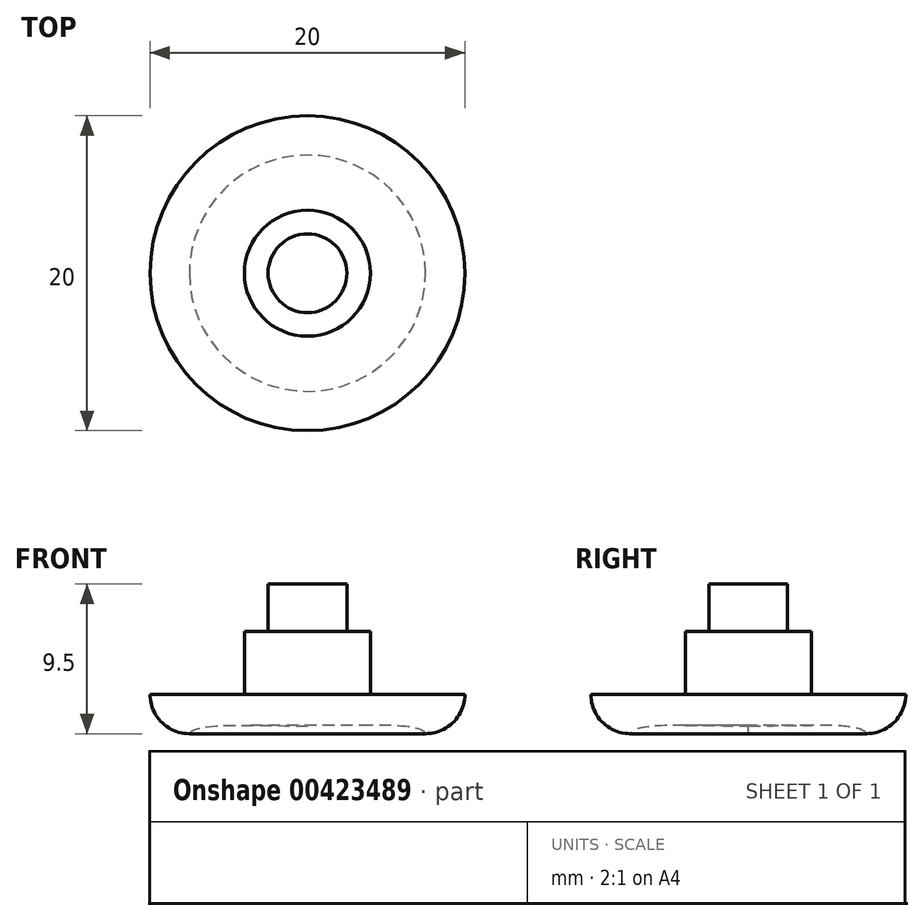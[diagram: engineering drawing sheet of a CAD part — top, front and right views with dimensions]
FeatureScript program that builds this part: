
annotation { "Feature Type Name" : "Feature", "Feature Type Description" : "" }
export const myFeature = defineFeature(function(context is Context, id is Id, definition is map)
    precondition{}
    {
        {
            var Q0;
            Q0=qCreatedBy(makeId("Front.planeOp"),FACE);
            var sketch = newSketch(context, id + "F0", { "sketchPlane" : qUnion([Q0])});
            skLineSegment(sketch, "E0.bottom", {"start": v(-4, 2) * mm, "end": v(4, 2) * mm});
            skLineSegment(sketch, "E0.left", {"start": v(-4, 2) * mm, "end": v(-4, -2) * mm});
            skPoint(sketch, "E0.middle", {"position": v(0, 0) * mm});
            skLineSegment(sketch, "E1", {"start": v(0, 2) * mm, "end": v(0, 5) * mm});
            skPoint(sketch, "E1.endSnap0", {"position": v(0, 2) * mm});
            skLineSegment(sketch, "E2", {"start": v(0, 5) * mm, "end": v(-2.5, 5) * mm});
            skLineSegment(sketch, "E3", {"start": v(-2.5, 5) * mm, "end": v(-2.5, 2) * mm});
            skLineSegment(sketch, "E4", {"start": v(0, -2) * mm, "end": v(-10, -2) * mm});
            skLineSegment(sketch, "E5", {"start": v(0, -2) * mm, "end": v(0, -4) * mm});
            skLineSegment(sketch, "E6", {"start": v(0, 2) * mm, "end": v(0, -2) * mm});
            skLineSegment(sketch, "E7.MirrorCS", {"start": v(0, -2) * mm, "end": v(0, 0) * mm});
            skLineSegment(sketch, "E8", {"start": v(-2.5, 2) * mm, "end": v(0, 2) * mm});
            skLineSegment(sketch, "E9", {"start": v(-10, -2) * mm, "end": v(-10, -2) * mm});
            skPoint(sketch, "E10.visualSharp", {"position": v(-10, -4.5) * mm});
            skArc(sketch, "E10.filletArc", {"start": v(-10, -2) * mm, "mid": v(-9.27, -3.77) * mm, "end": v(-7.5, -4.5) * mm});
            skFitSpline(sketch, "E11", {"points": [v(-7.5, -4.5) * mm, v(0, -4) * mm], "startDerivative": vector(1, 2.2) * mm, "endDerivative": vector(11.01, 0) * mm});
            skSolve(sketch);
        }
        {
            var Q0;
            {var subQ0=sQuery(id+"F0.wireOp",EDGE,"E5");Q0=makeQuery(id+"F0.imprint","IMPRINT",FACE,{"disambiguationData":[TD([[makeQuery(id+"F0.imprint","IMPRINT",EDGE,{"derivedFrom":subQ0}),-1.0]])]});}
            var Q1;
            {var subQ1=sQuery(id+"F0.wireOp",EDGE,"E0.left");Q1=makeQuery(id+"F0.imprint","IMPRINT",FACE,{"disambiguationData":[TD([[makeQuery(id+"F0.imprint","IMPRINT",EDGE,{"derivedFrom":subQ1}),1.0]])]});}
            var Q2;
            {var subQ0=sQuery(id+"F0.wireOp",EDGE,"E1");Q2=makeQuery(id+"F0.imprint","IMPRINT",FACE,{"disambiguationData":[TD([[makeQuery(id+"F0.imprint","IMPRINT",EDGE,{"derivedFrom":subQ0}),1.0]])]});}
            var Q3;
            Q3=sQuery(id+"F0.wireOp",EDGE,"E6");
            revolve(context, id + "F1", {"entities" : qUnion([Q0, Q1, Q2]), "axis" : qUnion([Q3]), "revolveType" : RevolveType.FULL});
        }
    });
